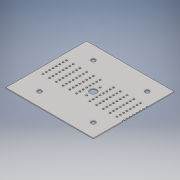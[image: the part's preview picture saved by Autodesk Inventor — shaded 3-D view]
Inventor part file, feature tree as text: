
AUTODESK INVENTOR PART (.ipt)
format: ipt  version: 2018 (Build 220112000, 112)  size: 297,984 bytes
history: native  units: in
note: dims shown in document units (in); Inventor stores cm internally (conversion verified against a paired STEP export)
features: extrude x5, sketch x5
ambient origin geometry x8: Origin, YZ Plane, XZ Plane, XY Plane, X Axis, Y Axis, Z Axis, Center Point
bodies: Solid1 (feature_tree)
feature tree (10):
  extrude  "Extrusion1"  Depth=0.125in
  extrude  "Extrusion2"  Depth=2.0in TaperAngle=0.0deg
  sketch  "Sketch3"  dims[d9=0.25in d11=0.25in]
  sketch  "Sketch4"  dims[d12=0.25in d13=0.25in d14=0.25in d15=0.25in]
  extrude  "Extrusion5"  Depth=0.25in
  extrude  "Extrusion6"  Depth=0.25in
  extrude  "Extrusion8"  Depth=0.5in
  sketch  "Sketch1"  dims[d2=0.125in d3=0.0in d4=6.0in]
  sketch  "Sketch2"  dims[d5=1.0in d6=2.0in d7=0.0in]
  sketch  "Sketch5"  dims[d56=0.25in d63=0.625in d67=8.0in d69=0.625in d70=0.625in d71=36.0in d72=0.0in d73=13.0in d74=13.0in d75=12.0in d77=0.25in d78=0.25in d79=0.25in d80=0.25in d81=0.25in d82=0.25in d83=0.5in d84=0.5in d85=0.5in d86=0.5in d87=0.5in d88=0.5in d89=0.25in d90=0.25in d91=0.25in d92=0.25in d93=0.25in d94=0.25in d95=0.25in d96=0.25in d97=0.25in d98=0.25in d99=0.25in d100=0.25in d101=0.25in d102=0.25in d103=0.25in d104=0.25in d105=0.25in d106=0.25in d107=0.25in d108=0.25in d109=0.25in d110=0.25in d111=0.25in d112=0.25in d113=0.5in d114=0.25in d115=0.25in d116=0.25in d117=0.25in d118=0.25in d119=0.25in d120=0.5in d121=0.25in d122=0.25in d123=0.25in d124=0.25in d125=0.25in d126=0.25in d127=0.5in d128=0.5in d130=0.25in d131=3.0in d132=0.0in d135=3.0in d136=0.0in]
